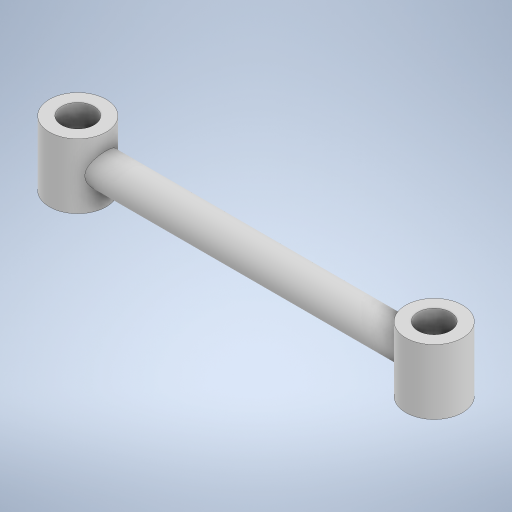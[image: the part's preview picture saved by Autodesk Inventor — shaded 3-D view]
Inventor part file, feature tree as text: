
AUTODESK INVENTOR PART (.ipt)
format: ipt  version: 2024 (Build 280153000, 153)  size: 264,704 bytes
history: native  units: in
note: dims shown in document units (in); Inventor stores cm internally (conversion verified against a paired STEP export)
features: sketch x3, extrude x3, revolve x1, mirror x1
ambient origin geometry x8: Origin, YZ Plane, XZ Plane, XY Plane, X Axis, Y Axis, Z Axis, Center Point
bodies: Solid1 (feature_tree)
feature tree (8):
  revolve  "Revolution1"  [1 undecoded]
  sketch  "Sketch2"  dims[d2=90.0deg d3=0.7874in]
  extrude  "Extrusion1"  Depth=0.7874in
  extrude  "Extrusion2"  Depth=1.5748in TaperAngle=0.0deg
  mirror  "Mirror1"
  extrude  "Extrusion3"  Depth=1.5748in TaperAngle=0.0deg
  sketch  "Sketch1"  dims[d0=8.6614in d1=0.3937in]
  sketch  "Sketch3"  dims[d4=1.378in d5=1.5748in d6=0.0in d7=1.5748in d8=0.0in d9=0.7874in d10=1.5748in d11=0.0in]
note: 1 required parameter value undecoded (feature->parameter linkage not recoverable at this tier; creation-order binding heuristic only, values carry confidence <= 0.55)
